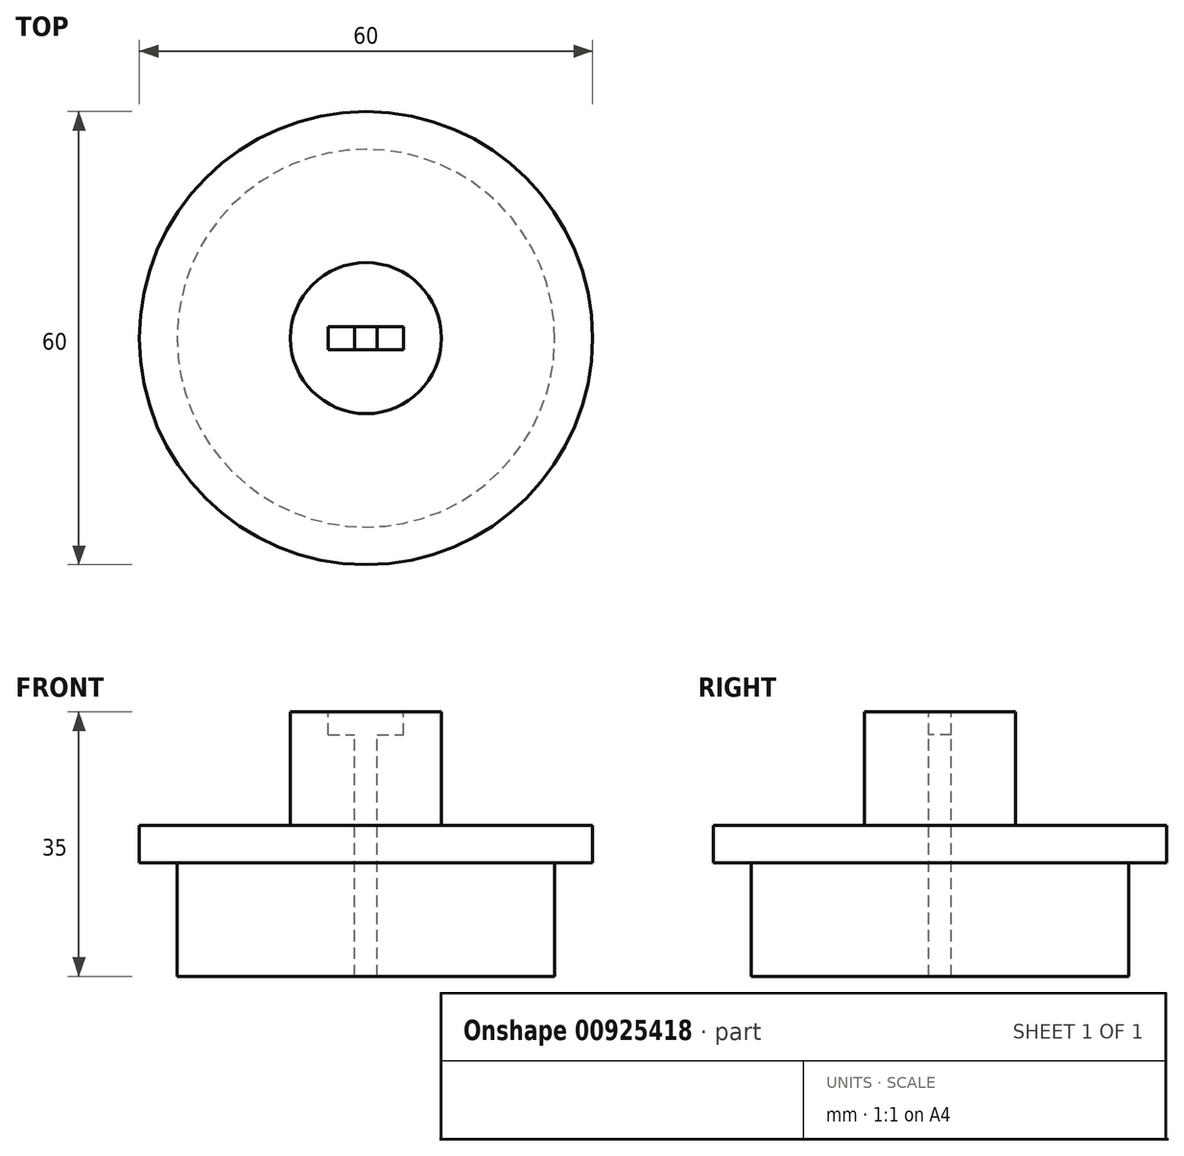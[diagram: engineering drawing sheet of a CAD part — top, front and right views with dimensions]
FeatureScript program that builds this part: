
annotation { "Feature Type Name" : "Feature", "Feature Type Description" : "" }
export const myFeature = defineFeature(function(context is Context, id is Id, definition is map)
    precondition{}
    {
        {
            var Q0;
            Q0=qCreatedBy(makeId("Front.planeOp"),FACE);
            var sketch = newSketch(context, id + "F0", { "sketchPlane" : qUnion([Q0])});
            skLineSegment(sketch, "E0", {"start": v(0, 26.1) * mm, "end": v(0, -21.35) * mm, "construction": true});
            skLineSegment(sketch, "E1", {"start": v(-1.5, 13.73) * mm, "end": v(-10, 13.73) * mm});
            skLineSegment(sketch, "E2", {"start": v(-10, 13.73) * mm, "end": v(-10, -1.27) * mm});
            skLineSegment(sketch, "E3", {"start": v(-10, -1.27) * mm, "end": v(-25, -1.27) * mm});
            skLineSegment(sketch, "E4", {"start": v(-25, -6.27) * mm, "end": v(-25, -21.27) * mm});
            skLineSegment(sketch, "E5", {"start": v(-25, -21.27) * mm, "end": v(0, -21.27) * mm});
            skLineSegment(sketch, "E6", {"start": v(0, 9.62) * mm, "end": v(0, -21.27) * mm});
            skLineSegment(sketch, "E7", {"start": v(-1.5, 13.73) * mm, "end": v(0, 13.73) * mm});
            skLineSegment(sketch, "E8", {"start": v(0, 13.73) * mm, "end": v(0, 9.62) * mm});
            skLineSegment(sketch, "E9", {"start": v(-25, -1.27) * mm, "end": v(-30, -1.27) * mm});
            skLineSegment(sketch, "E10", {"start": v(-30, -1.27) * mm, "end": v(-30, -6.27) * mm});
            skLineSegment(sketch, "E11", {"start": v(-30, -6.27) * mm, "end": v(-25, -6.27) * mm});
            skSolve(sketch);
        }
        {
            var Q0;
            Q0 = qSketchRegion(id + "F0", true);
            var Q1;
            Q1=sQuery(id+"F0.wireOp",EDGE,"E0");
            revolve(context, id + "F1", {"surfaceOperationType" : NewSurfaceOperationType.NEW, "entities" : qUnion([Q0]), "axis" : qUnion([Q1]), "revolveType" : RevolveType.FULL});
        }
        {
            var Q0;
            Q0=makeQuery(id+"F1.opRevolve","SWEPT_FACE",FACE,{"disambiguationData":[OSD([sQuery(id+"F0.wireOp",EDGE,"E1"),sQuery(id+"F0.wireOp",EDGE,"E7")])]});
            var sketch = newSketch(context, id + "F2", { "sketchPlane" : qUnion([Q0])});
            skLineSegment(sketch, "E12.bottom", {"start": v(-5, 1.5) * mm, "end": v(5, 1.5) * mm});
            skLineSegment(sketch, "E12.top", {"start": v(-5, -1.5) * mm, "end": v(5, -1.5) * mm});
            skLineSegment(sketch, "E12.left", {"start": v(-5, 1.5) * mm, "end": v(-5, -1.5) * mm});
            skLineSegment(sketch, "E12.right", {"start": v(5, 1.5) * mm, "end": v(5, -1.5) * mm});
            skPoint(sketch, "E12.middle", {"position": v(0, 0) * mm});
            skSolve(sketch);
        }
        {
            var Q0;
            Q0 = qSketchRegion(id + "F2", true);
            extrude(context, id + "F3", {"entities" : qUnion([Q0]), "operationType" : NewBodyOperationType.REMOVE, "oppositeDirection" : true, "depth" : 3 * mm, "offsetDistance" : 25 * mm});
        }
        {
            var Q0;
            Q0=makeQuery(id+"F3.boolean.opBoolean","COPY",FACE,{"derivedFrom":makeQuery(id+"F3.opExtrude","CAP_FACE",FACE,{"disambiguationData":[OSD([sQuery(id+"F2.wireOp",EDGE,"E12.bottom"),sQuery(id+"F2.wireOp",EDGE,"E12.top"),sQuery(id+"F2.wireOp",EDGE,"E12.left"),sQuery(id+"F2.wireOp",EDGE,"E12.right")])],"isStart":false})});
            var sketch = newSketch(context, id + "F4", { "sketchPlane" : qUnion([Q0])});
            skLineSegment(sketch, "E13.bottom", {"start": v(-1.5, 1.5) * mm, "end": v(1.5, 1.5) * mm});
            skLineSegment(sketch, "E13.top", {"start": v(-1.5, -1.5) * mm, "end": v(1.5, -1.5) * mm});
            skLineSegment(sketch, "E13.left", {"start": v(-1.5, 1.5) * mm, "end": v(-1.5, -1.5) * mm});
            skLineSegment(sketch, "E13.right", {"start": v(1.5, 1.5) * mm, "end": v(1.5, -1.5) * mm});
            skPoint(sketch, "E13.middle", {"position": v(0, 0) * mm});
            skSolve(sketch);
        }
        {
            var Q0;
            Q0 = qSketchRegion(id + "F4", true);
            extrude(context, id + "F5", {"entities" : qUnion([Q0]), "operationType" : NewBodyOperationType.REMOVE, "oppositeDirection" : true, "depth" : 40 * mm, "offsetDistance" : 25 * mm});
        }
    });
